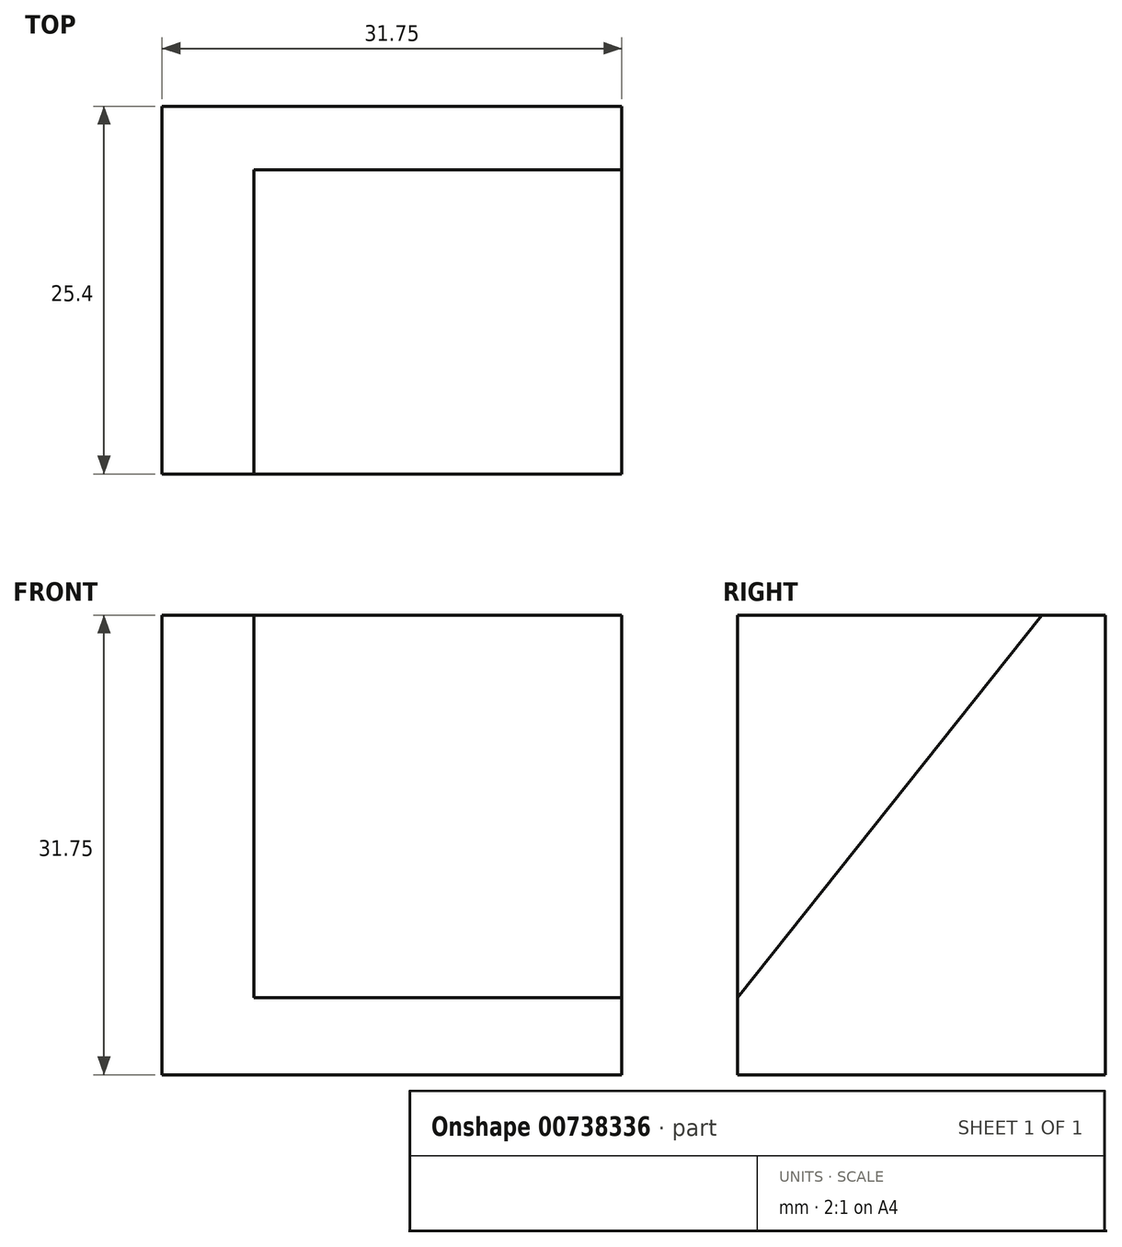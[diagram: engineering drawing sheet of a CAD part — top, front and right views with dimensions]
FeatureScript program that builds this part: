
annotation { "Feature Type Name" : "Feature", "Feature Type Description" : "" }
export const myFeature = defineFeature(function(context is Context, id is Id, definition is map)
    precondition{}
    {
        {
            var Q0;
            Q0=qCreatedBy(makeId("Top.planeOp"),FACE);
            var sketch = newSketch(context, id + "F0", { "sketchPlane" : qUnion([Q0])});
            skLineSegment(sketch, "E0", {"start": v(0, 0) * mm, "end": v(0, 25.4) * mm});
            skLineSegment(sketch, "E1", {"start": v(0, 25.4) * mm, "end": v(31.75, 25.4) * mm});
            skLineSegment(sketch, "E2", {"start": v(31.75, 25.4) * mm, "end": v(31.75, 0) * mm});
            skLineSegment(sketch, "E3", {"start": v(31.75, 0) * mm, "end": v(0, 0) * mm});
            skSolve(sketch);
        }
        {
            var Q0;
            Q0 = qSketchRegion(id + "F0", true);
            extrude(context, id + "F1", {"entities" : qUnion([Q0]), "depth" : 31.75 * mm, "offsetDistance" : 25.4 * mm});
        }
        {
            var Q0;
            Q0=makeQuery(id+"F1.opExtrude","SWEPT_FACE",FACE,{"disambiguationData":[OSD([sQuery(id+"F0.wireOp",EDGE,"E2")])]});
            var sketch = newSketch(context, id + "F2", { "sketchPlane" : qUnion([Q0])});
            skLineSegment(sketch, "E4", {"start": v(21, 31.75) * mm, "end": v(0, 5.33) * mm});
            skLineSegment(sketch, "E5", {"start": v(0, 5.33) * mm, "end": v(0, 31.75) * mm});
            skLineSegment(sketch, "E6", {"start": v(0, 31.75) * mm, "end": v(21, 31.75) * mm});
            skSolve(sketch);
        }
        {
            var Q0;
            Q0 = qSketchRegion(id + "F2", true);
            extrude(context, id + "F3", {"entities" : qUnion([Q0]), "operationType" : NewBodyOperationType.REMOVE, "oppositeDirection" : true, "depth" : 25.4 * mm, "offsetDistance" : 25.4 * mm});
        }
    });
